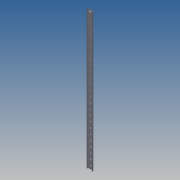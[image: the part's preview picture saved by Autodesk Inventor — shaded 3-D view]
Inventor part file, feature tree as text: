
AUTODESK INVENTOR PART (.ipt)
format: ipt  version: 2011 (Build 150239000, 239)  size: 275,456 bytes
history: native  units: mm
features: extrude x6, fillet x6, sketch x6
ambient origin geometry x8: Origin, YZ Plane, XZ Plane, XY Plane, X Axis, Y Axis, Z Axis, Center Point
feature tree (18):
  extrude  "Extrusion10"  Depth=510.0mm TaperAngle=0.0deg
  extrude  "Extrusion11"  Depth=1.0mm
  extrude  "Extrusion12"  Depth=5.0mm
  fillet  "Fillet12"  Radius=6.799998mm
  fillet  "Fillet13"  Radius=5.0mm
  fillet  "Fillet14"  Radius=6.799998mm
  fillet  "Fillet15"  Radius=4.5mm
  fillet  "Fillet16"  Radius=0.3mm
  fillet  "Fillet17"  Radius=0.3mm
  extrude  "Extrusion13"  Depth=0.1mm
  extrude  "Extrusion14"  Depth=1.0mm
  extrude  "Extrusion15"  Depth=20.0mm
  sketch  "Sketch1"  dims[d105=0.1mm d106=510.0mm d107=0.0mm]
  sketch  "Sketch12"  dims[d108=5.3mm d109=1.0mm]
  sketch  "Sketch13"  dims[d110=0.3mm d111=0.0mm d112=5.0mm d113=6.799998mm d115=5.0mm d116=6.799998mm d117=4.5mm d118=0.0mm d119=0.3mm d120=0.3mm]
  sketch  "Sketch14"  dims[d121=0.1mm d122=0.1mm]
  sketch  "Sketch15"  dims[d123=1.0mm d124=1.0mm]
  sketch  "Sketch16"  dims[d137=20.0mm d138=20.0mm d143=12.4mm d144=20.0mm d145=20.0mm d146=20.0mm d147=20.0mm d148=20.0mm d149=20.0mm d150=9.299998mm d151=9.299998mm d152=9.299998mm d153=9.299998mm d154=9.299998mm d155=9.299998mm d156=9.3mm d157=9.3mm d158=9.3mm d159=9.3mm d160=9.3mm d161=9.3mm d162=9.3mm d163=9.3mm d164=9.3mm d165=20.0mm d166=20.0mm d167=20.0mm d168=20.0mm d169=20.0mm d170=20.0mm d171=20.0mm d172=20.0mm d173=20.0mm d174=20.0mm d175=20.0mm d176=20.0mm d177=9.3mm d178=9.300002mm d179=9.3mm d180=9.3mm d181=20.0mm d182=20.0mm d183=9.3mm d184=20.0mm d185=2.0mm d186=0.0mm d193=1.0mm d194=0.0mm d196=5.0mm d198=100.0mm d199=100.0mm d200=100.0mm d201=100.0mm d202=55.0mm d203=1.7mm d204=1.7mm d205=1.7mm d206=1.7mm d207=1.7mm d208=1.7mm d209=1.0mm d210=0.0mm]
